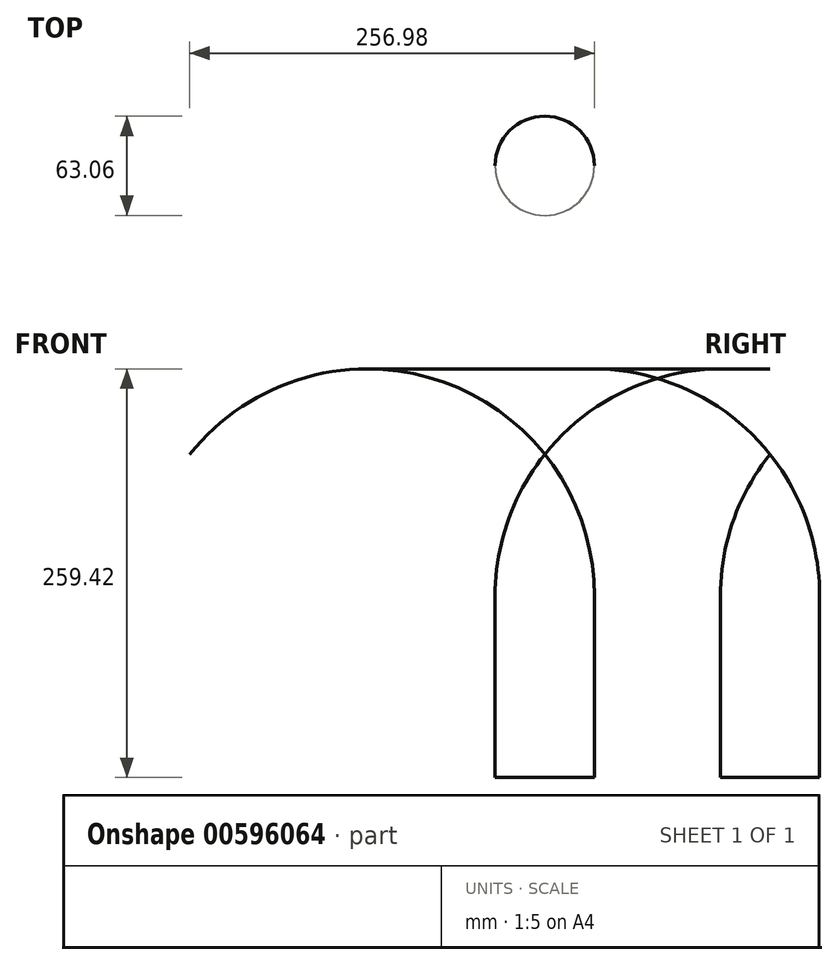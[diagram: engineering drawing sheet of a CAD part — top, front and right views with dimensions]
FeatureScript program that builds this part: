
annotation { "Feature Type Name" : "Feature", "Feature Type Description" : "" }
export const myFeature = defineFeature(function(context is Context, id is Id, definition is map)
    precondition{}
    {
        {
            var Q0;
            Q0=qCreatedBy(makeId("Right.planeOp"),FACE);
            var sketch = newSketch(context, id + "F0", { "sketchPlane" : qUnion([Q0])});
            skLineSegment(sketch, "E0.bottom", {"start": v(0, 0) * mm, "end": v(31.53, 0) * mm});
            skLineSegment(sketch, "E0.left", {"start": v(0, 0) * mm, "end": v(0, 115.17) * mm});
            skLineSegment(sketch, "E0.right", {"start": v(31.53, 0) * mm, "end": v(31.53, 115.17) * mm});
            skLineSegment(sketch, "E1", {"start": v(0, 115.17) * mm, "end": v(0, 205.18) * mm});
            skArc(sketch, "E2", {"start": v(31.53, 115.17) * mm, "mid": v(23.42, 162.86) * mm, "end": v(0, 205.18) * mm});
            skSolve(sketch);
        }
        {
            var Q0;
            Q0=makeQuery(id+"F0.imprint","IMPRINT",FACE,{"disambiguationData":[TD([[makeQuery(id+"F0.imprint","IMPRINT",EDGE,{"derivedFrom":sQuery(id+"F0.wireOp",EDGE,"E0.bottom")}),1.0]])]});
            var Q1;
            Q1=sQuery(id+"F0.wireOp",EDGE,"E0.left");
            revolve(context, id + "F1", {"entities" : qUnion([Q0]), "axis" : qUnion([Q1]), "revolveType" : RevolveType.FULL});
        }
    });
